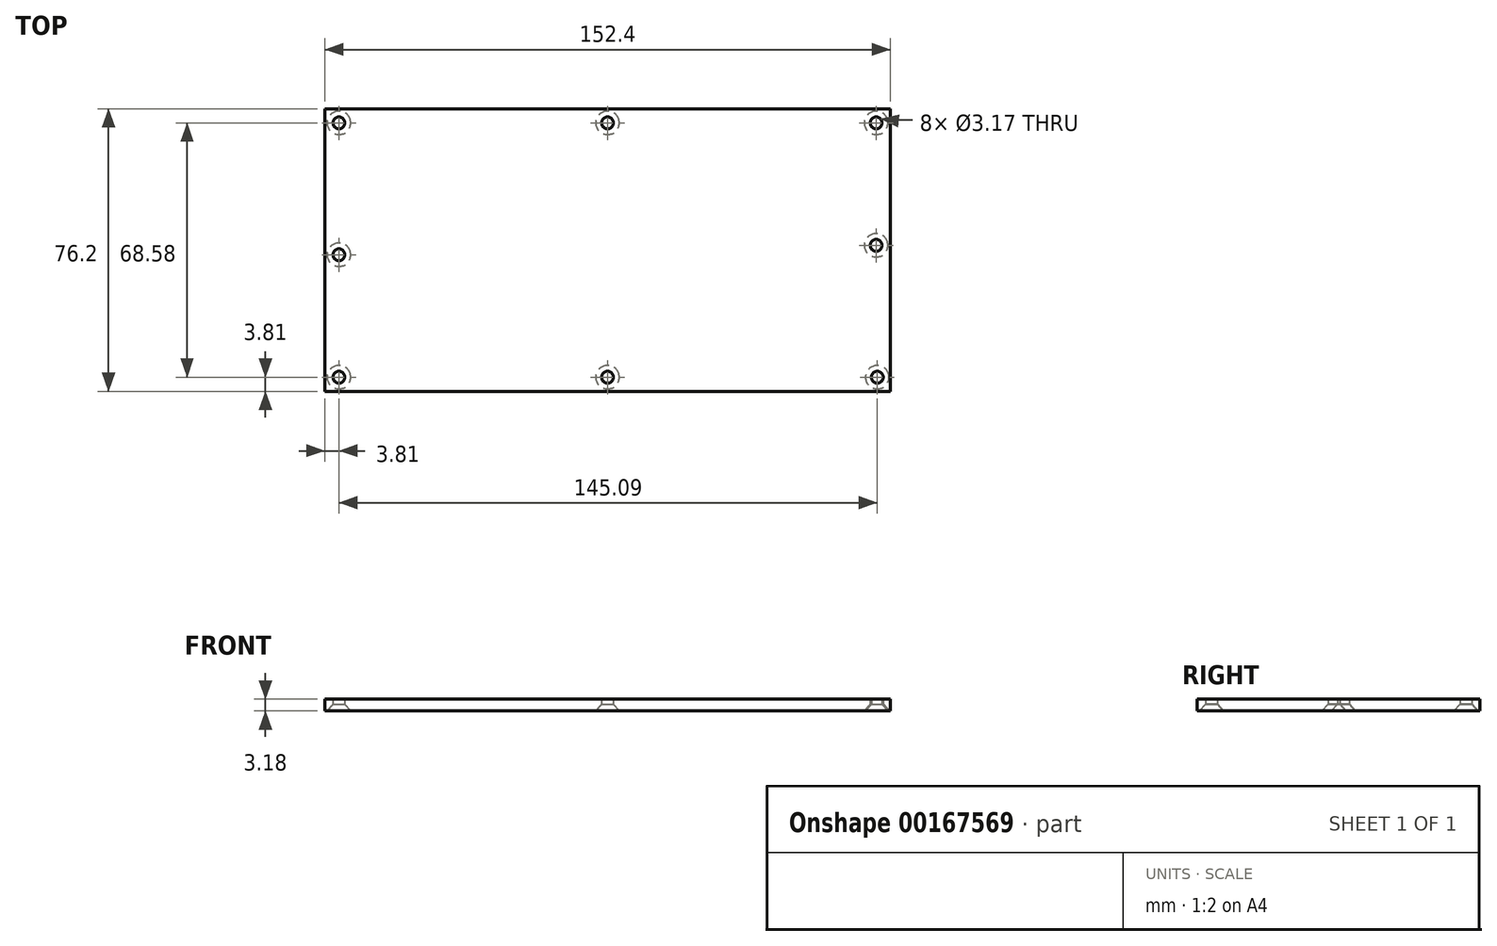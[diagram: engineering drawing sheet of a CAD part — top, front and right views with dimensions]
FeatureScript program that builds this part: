
annotation { "Feature Type Name" : "Feature", "Feature Type Description" : "" }
export const myFeature = defineFeature(function(context is Context, id is Id, definition is map)
    precondition{}
    {
        {
            var Q0;
            Q0=qCreatedBy(makeId("Top.planeOp"),FACE);
            var sketch = newSketch(context, id + "F0", { "sketchPlane" : qUnion([Q0])});
            skLineSegment(sketch, "E0.bottom", {"start": v(0, 0) * mm, "end": v(152.4, 0) * mm});
            skLineSegment(sketch, "E0.top", {"start": v(0, 76.2) * mm, "end": v(152.4, 76.2) * mm});
            skLineSegment(sketch, "E0.left", {"start": v(0, 0) * mm, "end": v(0, 76.2) * mm});
            skLineSegment(sketch, "E0.right", {"start": v(152.4, 0) * mm, "end": v(152.4, 76.2) * mm});
            skSolve(sketch);
        }
        {
            var Q0;
            Q0=qSketchRegion(id+"F0",true);
            extrude(context, id + "F1", {"entities" : qUnion([Q0]), "depth" : 3.17 * mm});
        }
        {
            var Q0;
            Q0=makeQuery(id+"F1.opExtrude","CAP_FACE",FACE,{"disambiguationData":[OSD([sQuery(id+"F0.wireOp",EDGE,"E0.bottom"),sQuery(id+"F0.wireOp",EDGE,"E0.top"),sQuery(id+"F0.wireOp",EDGE,"E0.left"),sQuery(id+"F0.wireOp",EDGE,"E0.right")])],"isStart":true});
            var sketch = newSketch(context, id + "F2", { "sketchPlane" : qUnion([Q0])});
            skPoint(sketch, "E1", {"position": v(3.81, -3.81) * mm});
            skPoint(sketch, "E2", {"position": v(3.81, -72.4) * mm});
            skPoint(sketch, "E3", {"position": v(148.6, -72.4) * mm});
            skPoint(sketch, "E4", {"position": v(148.59, -457.2) * mm});
            skPoint(sketch, "E5", {"position": v(3.81, -36.83) * mm});
            skPoint(sketch, "E6", {"position": v(148.6, -39.37) * mm});
            skPoint(sketch, "E7", {"position": v(76.2, -3.81) * mm});
            skPoint(sketch, "E7.positionSnap0", {"position": v(76.2, 0) * mm});
            skPoint(sketch, "E8", {"position": v(148.9, -3.81) * mm});
            skPoint(sketch, "E9", {"position": v(76.2, -72.4) * mm});
            skPoint(sketch, "E9.positionSnap0", {"position": v(76.2, -76.2) * mm});
            skSolve(sketch);
        }
        {
            var Q0;
            Q0=sQuery(id+"F2.wireOp",VERTEX,"E1");
            var Q1;
            Q1=sQuery(id+"F2.wireOp",VERTEX,"E5");
            var Q2;
            Q2=sQuery(id+"F2.wireOp",VERTEX,"E2");
            var Q3;
            Q3=sQuery(id+"F2.wireOp",VERTEX,"7487b3a6-acc1-4e90-beda-102a1c14b14c");
            var Q4;
            Q4=sQuery(id+"F2.wireOp",VERTEX,"E3");
            var Q5;
            Q5=sQuery(id+"F2.wireOp",VERTEX,"E6");
            var Q6;
            Q6=sQuery(id+"F2.wireOp",VERTEX,"E4");
            var Q7;
            Q7=sQuery(id+"F2.wireOp",VERTEX,"4811afb0-1995-4d04-a8f7-f19f3f342a0c");
            var Q8;
            Q8=sQuery(id+"F2.wireOp",VERTEX,"5cd4792d-c5bd-4e49-9294-18c8d0c74e96");
            var Q9;
            Q9=sQuery(id+"F2.wireOp",VERTEX,"E7");
            var Q10;
            Q10=sQuery(id+"F2.wireOp",VERTEX,"E9");
            var Q11;
            Q11=sQuery(id+"F2.wireOp",VERTEX,"E8");
            var Q12;
            Q12=makeQuery(id+"F1.opExtrude","SWEPT_BODY",BODY,{"disambiguationData":[OSD([sQuery(id+"F0.wireOp",EDGE,"E0.bottom"),sQuery(id+"F0.wireOp",EDGE,"E0.top"),sQuery(id+"F0.wireOp",EDGE,"E0.left"),sQuery(id+"F0.wireOp",EDGE,"E0.right")])]});
            hole(context, id + "F3", {"style" : HoleStyle.C_SINK, "endStyle" : HoleEndStyle.THROUGH, "holeDiameter" : 3.17 * mm, "cSinkDiameter" : 6.35 * mm, "cSinkAngle" : 82 * degree, "locations" : qUnion([Q0, Q1, Q2, Q3, Q4, Q5, Q6, Q7, Q8, Q9, Q10, Q11]), "scope" : qUnion([Q12]), "isTappedThrough" : true});
        }
    });
